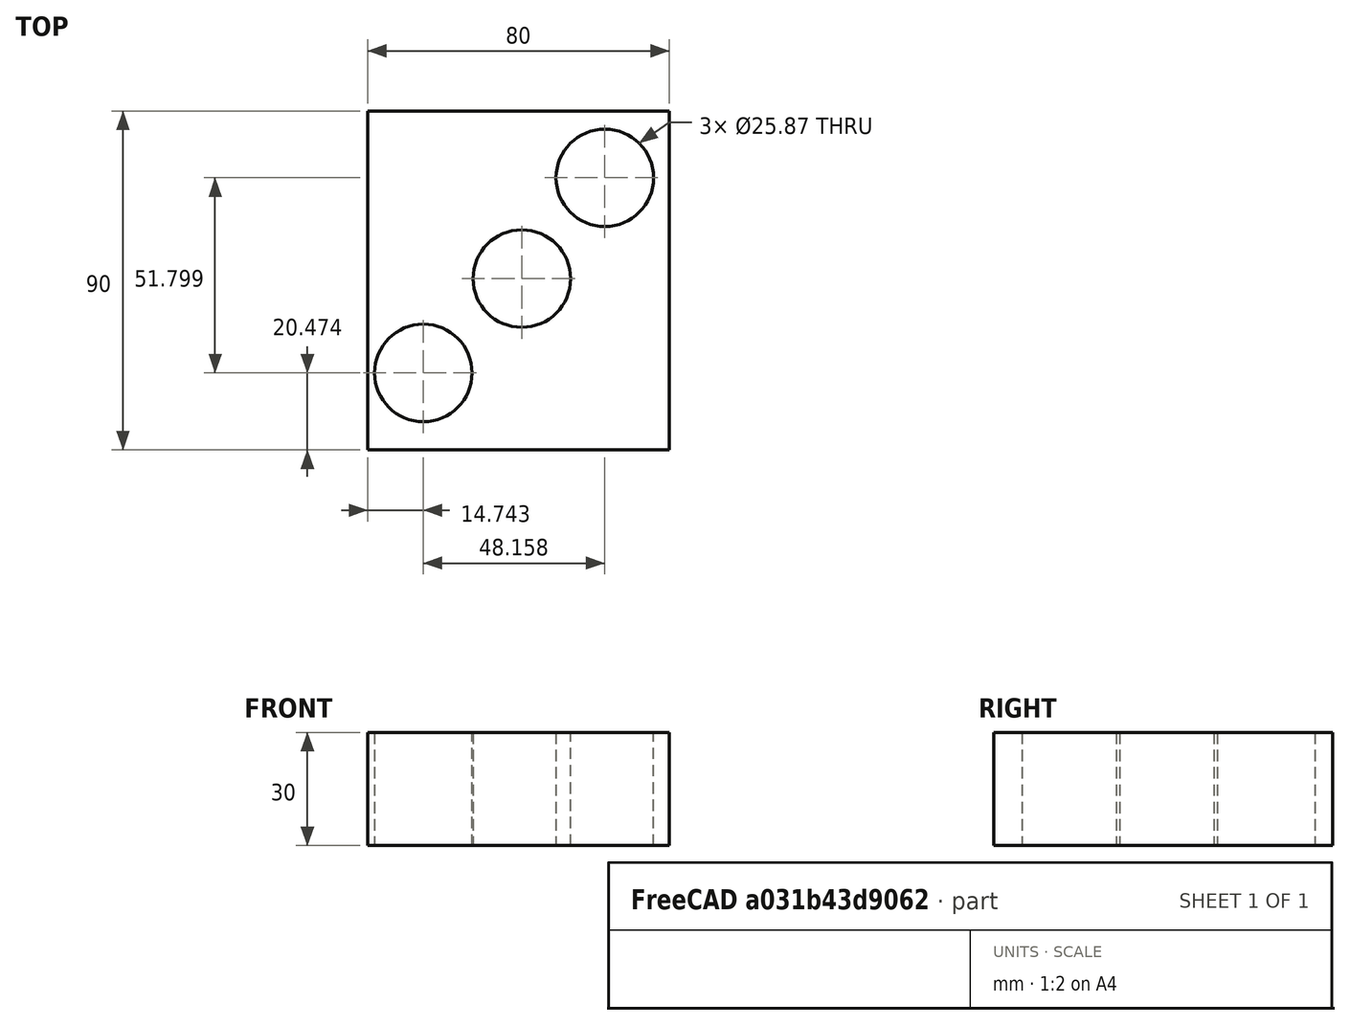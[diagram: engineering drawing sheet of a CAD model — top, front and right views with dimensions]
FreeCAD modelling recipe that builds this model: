
FCSTD DOCUMENT  (FreeCAD 0.18R16131 (Git))
Label: Momentum_Mold_Plate_30X80X150
License: All rights reserved
LicenseURL: http://en.wikipedia.org/wiki/All_rights_reserved
objects: Sketcher::SketchObject×1, PartDesign::Pad×1, PartDesign::Body×1
note: 4 computed .brp shape members not serialized (recipe doc carries the construction recipe); baked Part::Feature solids carry a one-line shape summary decoded from their .brp

FEATURE [Sketcher::SketchObject] Sketch
  MapMode = 5
  Support = -> [XY_Plane]
  sketch-geometry (7):
    g0: LineSegment StartX=-56.9576 StartY=8.68042 StartZ=0 EndX=23.0424 EndY=8.68042 EndZ=0
    g1: LineSegment StartX=23.0424 StartY=8.68042 StartZ=0 EndX=23.0424 EndY=98.6804 EndZ=0
    g2: LineSegment StartX=23.0424 StartY=98.6804 StartZ=0 EndX=-56.9576 EndY=98.6804 EndZ=0
    g3: LineSegment StartX=-56.9576 StartY=98.6804 StartZ=0 EndX=-56.9576 EndY=8.68042 EndZ=0
    g4: Circle CenterX=-42.2166 CenterY=29.154 CenterZ=0 NormalX=0 NormalY=0 NormalZ=1 AngleXU=0 Radius=12.9349
    g5: Circle CenterX=-16.0723 CenterY=54.191 CenterZ=0 NormalX=0 NormalY=0 NormalZ=1 AngleXU=0 Radius=12.9349
    g6: Circle CenterX=5.94154 CenterY=80.9529 CenterZ=0 NormalX=0 NormalY=0 NormalZ=1 AngleXU=0 Radius=12.9349
  constraints (10):
    c: Coincident(g0,g1)
    c: Coincident(g1,g2)
    c: Coincident(g2,g3)
    c: Coincident(g3,g0)
    c: Horizontal(g0)
    c: Horizontal(g2)
    c: Vertical(g1)
    c: Vertical(g3)
    c: DistanceX(g0,g0) = 80
    c: DistanceY(g1,g1) = 90
FEATURE [PartDesign::Pad] Pad
  Length = 30
  Length2 = 100
  Profile = -> Sketch
  Type = 0
FEATURE [PartDesign::Body] Body
  Group = -> [Sketch,Pad]
  Origin = -> Origin
  Tip = -> Pad
